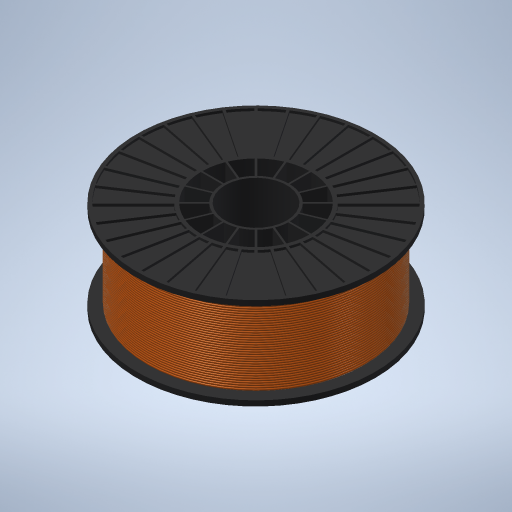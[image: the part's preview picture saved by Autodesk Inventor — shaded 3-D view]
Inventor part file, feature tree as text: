
AUTODESK INVENTOR PART (.ipt)
format: ipt  version: 2024 (Build 280153000, 153)  size: 1,126,400 bytes
history: native  units: mm
features: projected_geometry x10, extrude x7, pattern_circular x2, revolve x2, hole x1, mirror x1, pattern_linear x1
ambient origin geometry x8: Origin, YZ Plane, XZ Plane, XY Plane, X Axis, Y Axis, Z Axis, Center Point
bodies: Solid1 (feature_tree)
feature tree (24):
  extrude  "Extrusion1"  Depth=202.0mm
  hole  "Hole2"  [1 undecoded]
  extrude  "Extrusion3"  Depth=10.0mm
  extrude  "Extrusion4"  Depth=20.0mm
  pattern_circular  "Circular Pattern1"  [2 undecoded]
  extrude  "Extrusion5"  Depth=25.0mm TaperAngle=0.0deg
  extrude  "Extrusion6"  Depth=1.5mm
  pattern_circular  "Circular Pattern2"  [2 undecoded]
  mirror  "Mirror1"
  extrude  "Extrusion7"  Depth=160.0mm TaperAngle=360.0deg
  extrude  "Extrusion8"  Depth=3.0mm
  revolve  "Revolution1"  [1 undecoded]
  revolve  "Revolution2"  [1 undecoded]
  pattern_linear  "Rectangular Pattern1"  Spacing1=2.0mm  [1 undecoded]
  projected_geometry  "Projected Loop1"
  projected_geometry  "Projected Loop2"
  projected_geometry  "Projected Loop3"
  projected_geometry  "Projected Loop4"
  projected_geometry  "Projected Loop5"
  projected_geometry  "Projected Loop6"
  projected_geometry  "Projected Loop7"
  projected_geometry  "Project Cut Edges1"
  projected_geometry  "Project Cut Edges2"
  projected_geometry  "Project Cut Edges3"
note: 8 required parameter values undecoded (feature->parameter linkage not recoverable at this tier; creation-order binding heuristic only, values carry confidence <= 0.55)